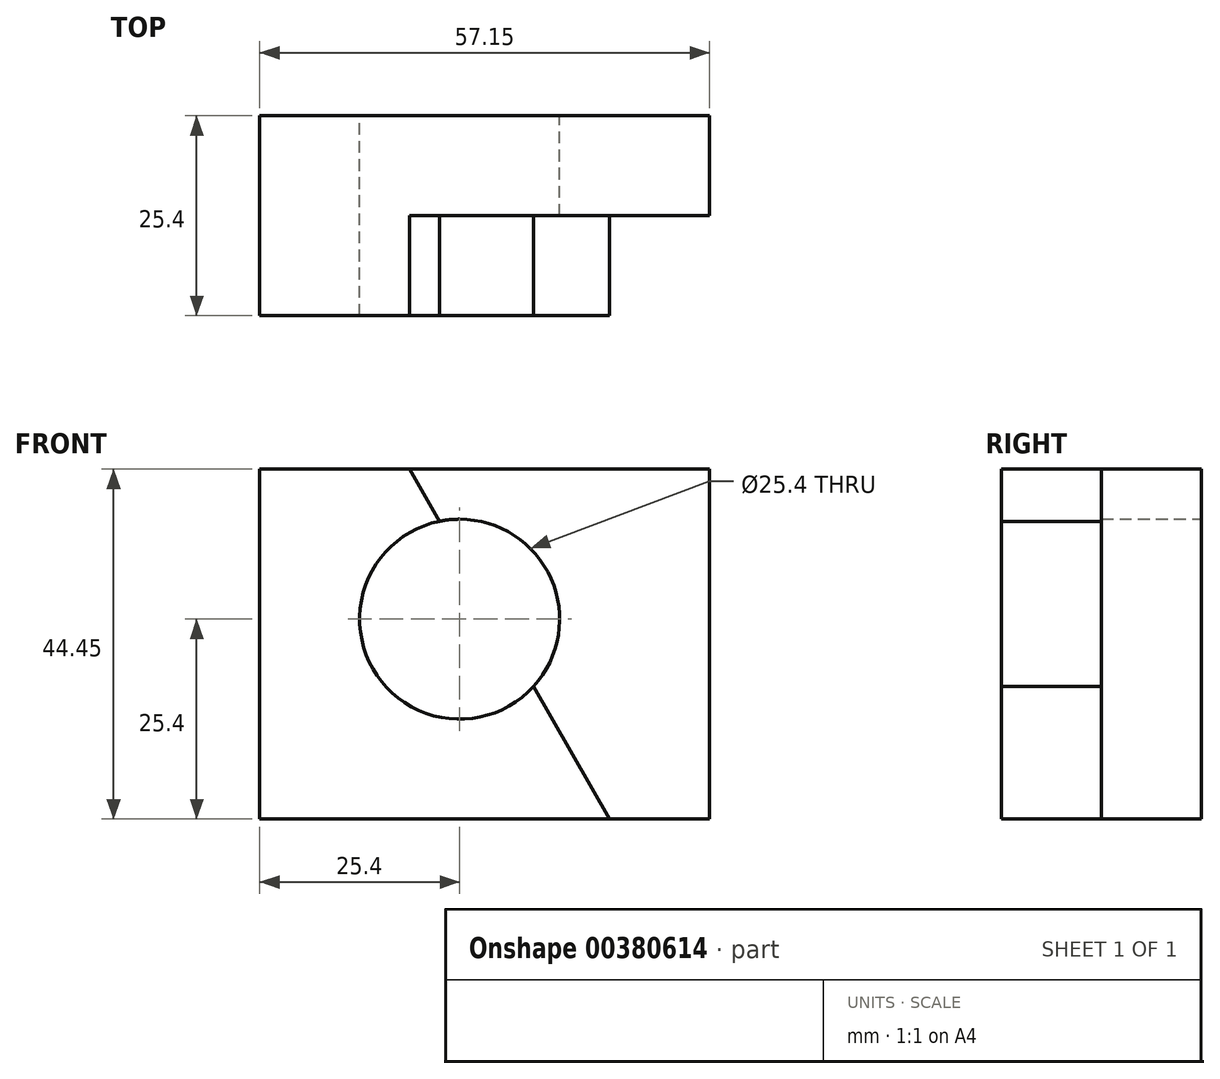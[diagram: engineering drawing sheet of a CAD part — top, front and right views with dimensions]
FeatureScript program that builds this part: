
annotation { "Feature Type Name" : "Feature", "Feature Type Description" : "" }
export const myFeature = defineFeature(function(context is Context, id is Id, definition is map)
    precondition{}
    {
        {
            var Q0;
            Q0=qCreatedBy(makeId("Front.planeOp"),FACE);
            var sketch = newSketch(context, id + "F0", { "sketchPlane" : qUnion([Q0])});
            skLineSegment(sketch, "E0", {"start": v(0, 0) * mm, "end": v(57.15, 0) * mm});
            skLineSegment(sketch, "E1", {"start": v(57.15, 0) * mm, "end": v(57.15, 44.45) * mm});
            skLineSegment(sketch, "E2", {"start": v(57.15, 44.45) * mm, "end": v(0, 44.45) * mm});
            skLineSegment(sketch, "E3", {"start": v(0, 44.45) * mm, "end": v(0, 0) * mm});
            skSolve(sketch);
        }
        {
            var Q0;
            Q0 = qSketchRegion(id + "F0", true);
            extrude(context, id + "F1", {"entities" : qUnion([Q0]), "depth" : 25.4 * mm});
        }
        {
            var Q0;
            Q0=makeQuery(id+"F1.opExtrude","CAP_FACE",FACE,{"disambiguationData":[OSD([sQuery(id+"F0.wireOp",EDGE,"E0"),sQuery(id+"F0.wireOp",EDGE,"E1"),sQuery(id+"F0.wireOp",EDGE,"E2"),sQuery(id+"F0.wireOp",EDGE,"E3")])],"isStart":false});
            var sketch = newSketch(context, id + "F2", { "sketchPlane" : qUnion([Q0])});
            skLineSegment(sketch, "E4", {"start": v(19.05, 44.45) * mm, "end": v(44.45, 0) * mm});
            skSolve(sketch);
        }
        {
            var Q0;
            {var subQ0=sQuery(id+"F2.wireOp",EDGE,"E4");Q0=makeQuery(id+"F2.imprint","IMPRINT",FACE,{"disambiguationData":[TD([[makeQuery(id+"F2.imprint","IMPRINT",EDGE,{"derivedFrom":subQ0}),1.0]])]});}
            extrude(context, id + "F3", {"entities" : qUnion([Q0]), "operationType" : NewBodyOperationType.REMOVE, "oppositeDirection" : true, "depth" : 12.7 * mm});
        }
        {
            var Q0;
            Q0=makeQuery(id+"F1.opExtrude","CAP_FACE",FACE,{"disambiguationData":[OSD([sQuery(id+"F0.wireOp",EDGE,"E0"),sQuery(id+"F0.wireOp",EDGE,"E1"),sQuery(id+"F0.wireOp",EDGE,"E2"),sQuery(id+"F0.wireOp",EDGE,"E3")])],"isStart":true});
            var sketch = newSketch(context, id + "F4", { "sketchPlane" : qUnion([Q0])});
            skCircle(sketch, "E5", {"center": v(-25.4, 25.4) * mm, "radius": 12.7 * mm});
            skSolve(sketch);
        }
        {
            var Q0;
            Q0=makeQuery(id+"F4.imprint","IMPRINT",FACE,{"disambiguationData":[TD([[makeQuery(id+"F4.imprint","IMPRINT",EDGE,{"derivedFrom":sQuery(id+"F4.wireOp",EDGE,"E5")}),1.0]])]});
            extrude(context, id + "F5", {"entities" : qUnion([Q0]), "operationType" : NewBodyOperationType.REMOVE, "oppositeDirection" : true, "depth" : 25.4 * mm});
        }
    });
